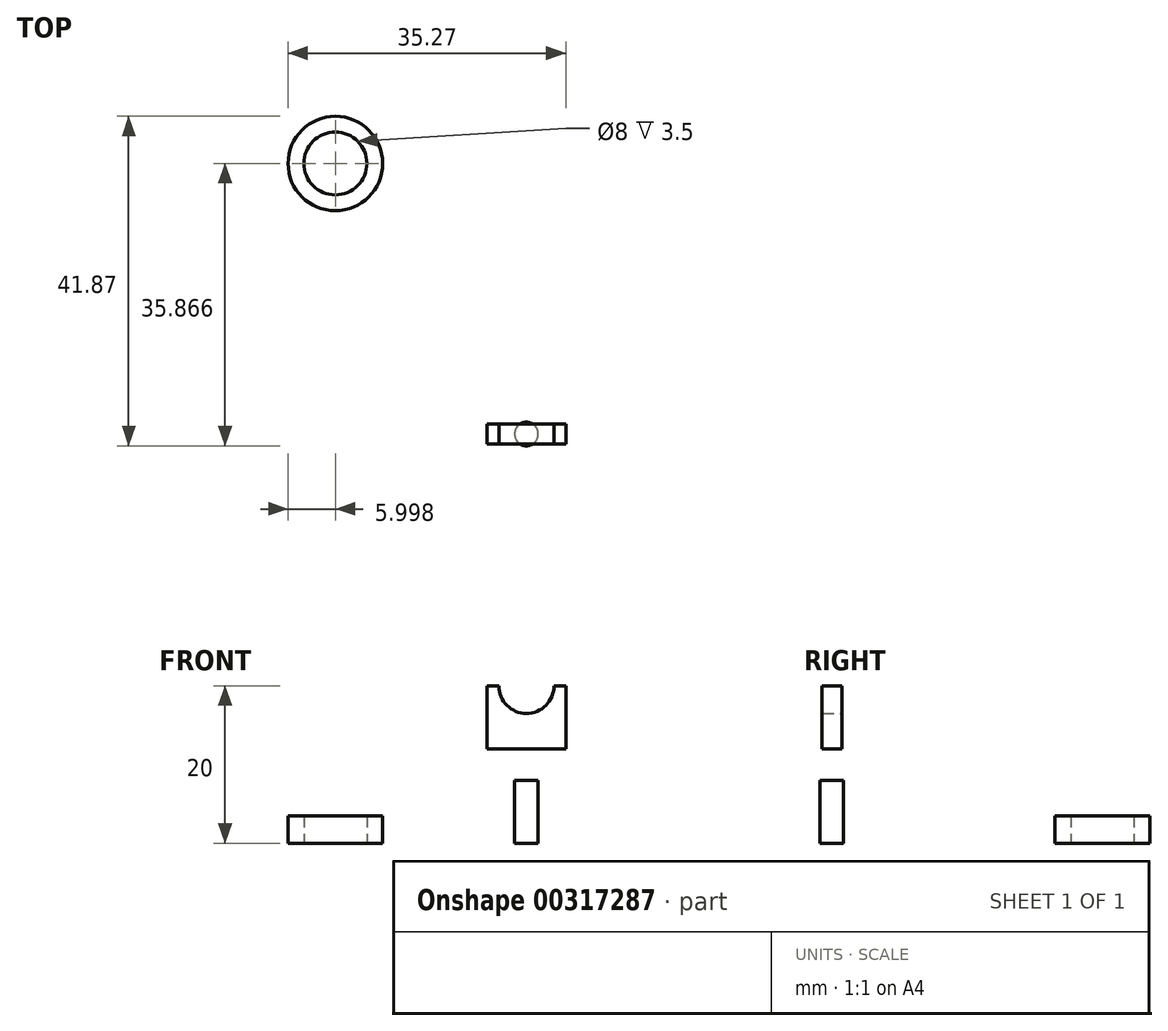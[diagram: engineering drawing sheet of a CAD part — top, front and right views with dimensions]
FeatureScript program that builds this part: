
annotation { "Feature Type Name" : "Feature", "Feature Type Description" : "" }
export const myFeature = defineFeature(function(context is Context, id is Id, definition is map)
    precondition{}
    {
        {
            var Q0;
            Q0=qCreatedBy(makeId("Front.planeOp"),FACE);
            var sketch = newSketch(context, id + "F0", { "sketchPlane" : qUnion([Q0])});
            skLineSegment(sketch, "E0", {"start": v(0, 30.58) * mm, "end": v(0, 12) * mm, "construction": true});
            skLineSegment(sketch, "E1.bottom", {"start": v(0, 0) * mm, "end": v(-4, 0) * mm});
            skLineSegment(sketch, "E1.right", {"start": v(-4, 0) * mm, "end": v(-4, 2) * mm});
            skLineSegment(sketch, "E2.bottom", {"start": v(-4, 2) * mm, "end": v(-5, 2) * mm});
            skLineSegment(sketch, "E2.top", {"start": v(0, 12) * mm, "end": v(-5, 12) * mm});
            skLineSegment(sketch, "E2.right", {"start": v(-5, 2) * mm, "end": v(-5, 12) * mm});
            skLineSegment(sketch, "E3.trimOffspring", {"start": v(0, 0) * mm, "end": v(0, -29.8) * mm, "construction": true});
            skLineSegment(sketch, "E4", {"start": v(0, 12) * mm, "end": v(0, 0) * mm});
            skLineSegment(sketch, "E5.MirrorCS", {"start": v(5, 2) * mm, "end": v(5, 12) * mm});
            skLineSegment(sketch, "E6.MirrorCS", {"start": v(0, 12) * mm, "end": v(5, 12) * mm});
            skLineSegment(sketch, "E7.bottom", {"start": v(-5, 12) * mm, "end": v(5, 12) * mm});
            skLineSegment(sketch, "E7.top", {"start": v(-5, 20) * mm, "end": v(5, 20) * mm});
            skLineSegment(sketch, "E7.left", {"start": v(-5, 12) * mm, "end": v(-5, 20) * mm});
            skLineSegment(sketch, "E7.right", {"start": v(5, 12) * mm, "end": v(5, 20) * mm});
            skArc(sketch, "E8", {"start": v(-5, 20) * mm, "mid": v(0, 25) * mm, "end": v(5, 20) * mm});
            skCircle(sketch, "E9", {"center": v(0, 20) * mm, "radius": 3.5 * mm});
            skLineSegment(sketch, "E10.bottom", {"start": v(0, 8) * mm, "end": v(-1.5, 8) * mm});
            skLineSegment(sketch, "E10.top", {"start": v(0, 0) * mm, "end": v(-1.5, 0) * mm});
            skLineSegment(sketch, "E10.left", {"start": v(0, 8) * mm, "end": v(0, 0) * mm});
            skLineSegment(sketch, "E10.right", {"start": v(-1.5, 8) * mm, "end": v(-1.5, 0) * mm});
            skSolve(sketch);
        }
        {
            var Q0;
            Q0=makeQuery(id+"F0.imprint","IMPRINT",FACE,{"disambiguationData":[TD([[makeQuery(id+"F0.imprint","IMPRINT",EDGE,{"derivedFrom":sQuery(id+"F0.wireOp",EDGE,"E1.bottom")}),-1.0]])]});
            var Q1;
            Q1=sQuery(id+"F0.wireOp",EDGE,"E3.trimOffspring");
            revolve(context, id + "F1", {"entities" : qUnion([Q0]), "axis" : qUnion([Q1]), "revolveType" : RevolveType.FULL});
        }
        {
            var Q0;
            {var subQ0=sQuery(id+"F0.wireOp",EDGE,"E8");Q0=makeQuery(id+"F0.imprint","IMPRINT",FACE,{"disambiguationData":[TD([[makeQuery(id+"F0.imprint","IMPRINT",EDGE,{"derivedFrom":subQ0}),-1.0]])]});}
            var Q1;
            {var subQ5=sQuery(id+"F0.wireOp",EDGE,"E7.left");Q1=makeQuery(id+"F0.imprint","IMPRINT",FACE,{"disambiguationData":[TD([[makeQuery(id+"F0.imprint","IMPRINT",EDGE,{"derivedFrom":subQ5}),-1.0]])]});}
            extrude(context, id + "F2", {"entities" : qUnion([Q0, Q1]), "operationType" : NewBodyOperationType.ADD, "endBound" : BoundingType.SYMMETRIC, "depth" : 2.5 * mm});
        }
        {
            var Q0;
            Q0=qCreatedBy(makeId("Top.planeOp"),FACE);
            var sketch = newSketch(context, id + "F3", { "sketchPlane" : qUnion([Q0])});
            skCircle(sketch, "E11", {"center": v(-24.27, 34.37) * mm, "radius": 6 * mm});
            skCircle(sketch, "E12", {"center": v(-24.27, 34.37) * mm, "radius": 4 * mm});
            skSolve(sketch);
        }
        {
            var Q0;
            Q0=makeQuery(id+"F3.imprint","IMPRINT",FACE,{"disambiguationData":[TD([[makeQuery(id+"F3.imprint","IMPRINT",EDGE,{"derivedFrom":sQuery(id+"F3.wireOp",EDGE,"E11")}),1.0]])]});
            extrude(context, id + "F4", {"entities" : qUnion([Q0]), "depth" : 3.5 * mm});
        }
    });
